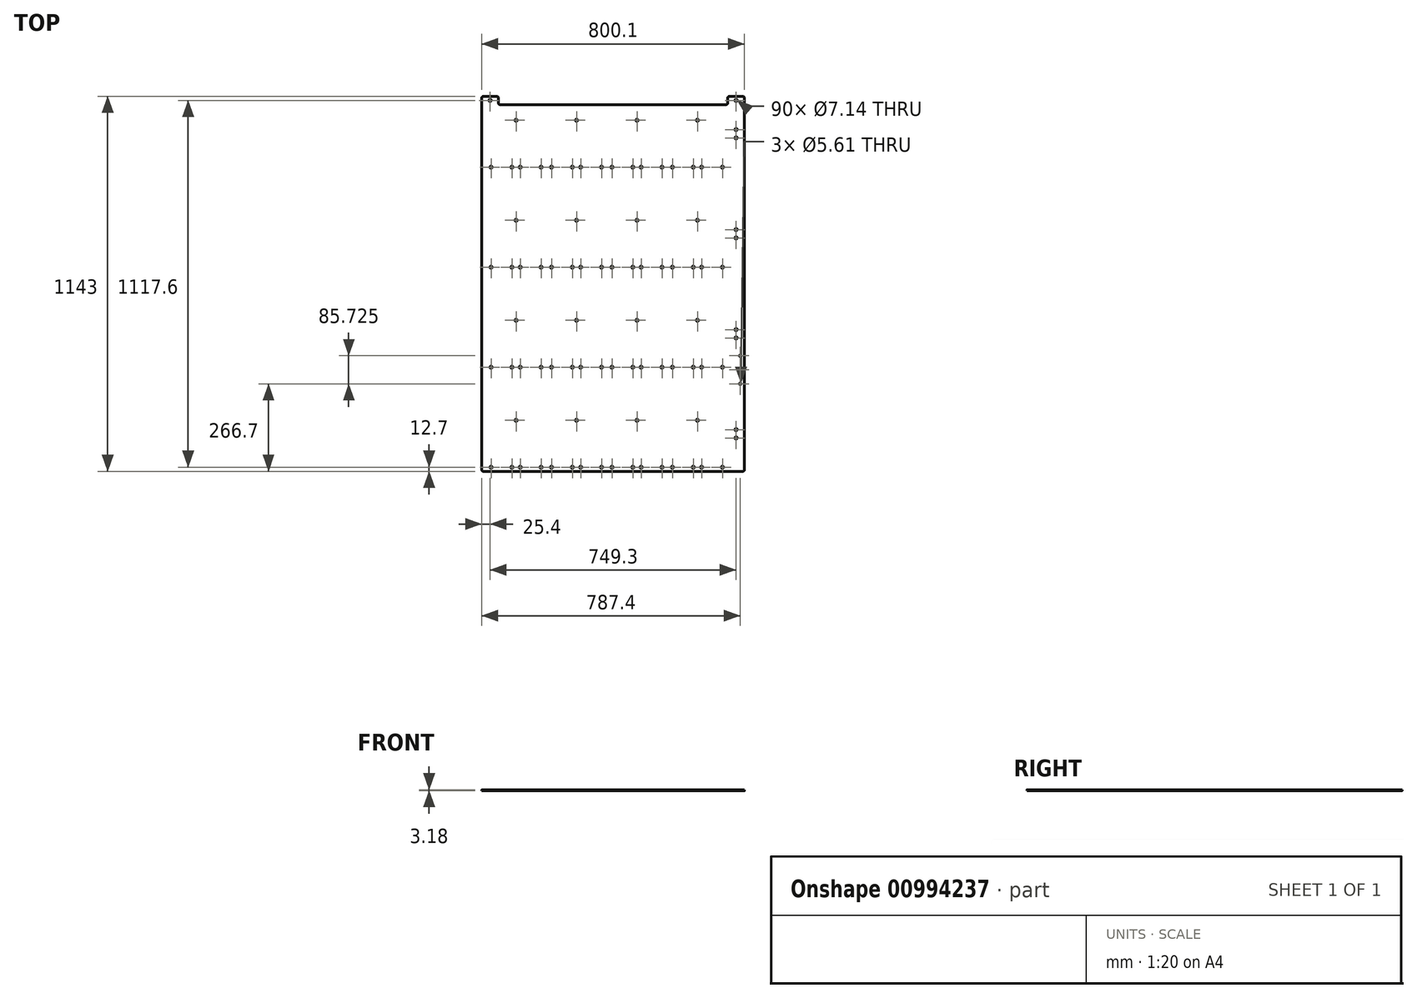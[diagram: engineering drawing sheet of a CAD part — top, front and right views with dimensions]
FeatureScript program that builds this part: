
annotation { "Feature Type Name" : "Feature", "Feature Type Description" : "" }
export const myFeature = defineFeature(function(context is Context, id is Id, definition is map)
    precondition{}
    {
        {
            var Q0;
            Q0=qCreatedBy(makeId("Top.planeOp"),FACE);
            var sketch = newSketch(context, id + "F0", { "sketchPlane" : qUnion([Q0])});
            skLineSegment(sketch, "E0.bottom", {"start": v(0, 0) * mm, "end": v(800.1, 0) * mm});
            skLineSegment(sketch, "E0.top", {"start": v(0, 1181.1) * mm, "end": v(800.1, 1181.1) * mm});
            skLineSegment(sketch, "E0.left", {"start": v(0, 0) * mm, "end": v(0, 1181.1) * mm});
            skLineSegment(sketch, "E0.right", {"start": v(800.1, 0) * mm, "end": v(800.1, 1181.1) * mm});
            skLineSegment(sketch, "E1", {"start": v(25.4, 1181.1) * mm, "end": v(25.4, 0) * mm, "construction": true});
            skLineSegment(sketch, "E2", {"start": v(698.5, 1181.1) * mm, "end": v(698.5, 0) * mm, "construction": true});
            skLineSegment(sketch, "E3", {"start": v(0, 1155.7) * mm, "end": v(800.1, 1155.7) * mm, "construction": true});
            skLineSegment(sketch, "E4", {"start": v(0, 571.5) * mm, "end": v(800.1, 571.5) * mm, "construction": true});
            skLineSegment(sketch, "E5", {"start": v(0, 279.4) * mm, "end": v(800.1, 279.4) * mm, "construction": true});
            skPoint(sketch, "E6", {"position": v(92.08, 965.2) * mm});
            skPoint(sketch, "E7.0.1.0", {"position": v(92.08, 660.4) * mm});
            skPoint(sketch, "E7.0.2.0", {"position": v(92.08, 355.6) * mm});
            skPoint(sketch, "E7.0.3.0", {"position": v(92.08, 50.8) * mm});
            skPoint(sketch, "E7.1.0.0", {"position": v(276.23, 965.2) * mm});
            skPoint(sketch, "E7.1.1.0", {"position": v(276.23, 660.4) * mm});
            skPoint(sketch, "E7.1.2.0", {"position": v(276.23, 355.6) * mm});
            skPoint(sketch, "E7.1.3.0", {"position": v(276.23, 50.8) * mm});
            skPoint(sketch, "E7.2.0.0", {"position": v(460.38, 965.2) * mm});
            skPoint(sketch, "E7.2.1.0", {"position": v(460.38, 660.4) * mm});
            skPoint(sketch, "E7.2.2.0", {"position": v(460.38, 355.6) * mm});
            skPoint(sketch, "E7.2.3.0", {"position": v(460.38, 50.8) * mm});
            skPoint(sketch, "E7.3.0.0", {"position": v(644.52, 965.2) * mm});
            skPoint(sketch, "E7.3.1.0", {"position": v(644.52, 660.4) * mm});
            skPoint(sketch, "E7.3.2.0", {"position": v(644.53, 355.6) * mm});
            skPoint(sketch, "E7.3.3.0", {"position": v(644.53, 50.8) * mm});
            skLineSegment(sketch, "E7.direction1", {"start": v(92.08, 965.2) * mm, "end": v(276.23, 965.2) * mm, "construction": true});
            skLineSegment(sketch, "E7.direction2", {"start": v(92.08, 965.2) * mm, "end": v(92.08, 660.4) * mm, "construction": true});
            skPoint(sketch, "E8", {"position": v(117.48, 965.2) * mm});
            skPoint(sketch, "E9.0.1.0", {"position": v(117.48, 660.4) * mm});
            skPoint(sketch, "E9.0.2.0", {"position": v(117.48, 355.6) * mm});
            skPoint(sketch, "E9.0.3.0", {"position": v(117.48, 50.8) * mm});
            skPoint(sketch, "E9.1.0.0", {"position": v(301.63, 965.2) * mm});
            skPoint(sketch, "E9.1.1.0", {"position": v(301.63, 660.4) * mm});
            skPoint(sketch, "E9.1.2.0", {"position": v(301.63, 355.6) * mm});
            skPoint(sketch, "E9.1.3.0", {"position": v(301.63, 50.8) * mm});
            skPoint(sketch, "E9.2.0.0", {"position": v(485.78, 965.2) * mm});
            skPoint(sketch, "E9.2.1.0", {"position": v(485.78, 660.4) * mm});
            skPoint(sketch, "E9.2.2.0", {"position": v(485.78, 355.6) * mm});
            skPoint(sketch, "E9.2.3.0", {"position": v(485.78, 50.8) * mm});
            skPoint(sketch, "E9.3.0.0", {"position": v(669.92, 965.2) * mm});
            skPoint(sketch, "E9.3.1.0", {"position": v(669.92, 660.4) * mm});
            skPoint(sketch, "E9.3.2.0", {"position": v(669.93, 355.6) * mm});
            skPoint(sketch, "E9.3.3.0", {"position": v(669.93, 50.8) * mm});
            skLineSegment(sketch, "E9.direction1", {"start": v(117.48, 965.2) * mm, "end": v(301.63, 965.2) * mm, "construction": true});
            skLineSegment(sketch, "E9.direction2", {"start": v(117.48, 965.2) * mm, "end": v(117.48, 660.4) * mm, "construction": true});
            skPoint(sketch, "E10", {"position": v(25.4, 1168.4) * mm});
            skPoint(sketch, "E11", {"position": v(774.7, 1168.4) * mm});
            skPoint(sketch, "E12", {"position": v(774.7, 1079.5) * mm});
            skPoint(sketch, "E13", {"position": v(774.7, 1054.1) * mm});
            skPoint(sketch, "E14.0.1.0", {"position": v(774.7, 774.7) * mm});
            skPoint(sketch, "E14.0.1.1", {"position": v(774.7, 749.3) * mm});
            skPoint(sketch, "E14.0.2.0", {"position": v(774.7, 469.9) * mm});
            skPoint(sketch, "E14.0.2.1", {"position": v(774.7, 444.5) * mm});
            skPoint(sketch, "E14.0.3.0", {"position": v(774.7, 165.1) * mm});
            skPoint(sketch, "E14.0.3.1", {"position": v(774.7, 139.7) * mm});
            skLineSegment(sketch, "E14.direction1", {"start": v(774.7, 1054.1) * mm, "end": v(800.1, 1054.1) * mm, "construction": true});
            skLineSegment(sketch, "E14.direction2", {"start": v(774.7, 1054.1) * mm, "end": v(774.7, 749.3) * mm, "construction": true});
            skPoint(sketch, "E15", {"position": v(787.4, 304.8) * mm});
            skPoint(sketch, "E16", {"position": v(787.4, 347.66) * mm});
            skPoint(sketch, "E17", {"position": v(787.4, 390.52) * mm});
            skLineSegment(sketch, "E18", {"start": v(104.77, 1155.7) * mm, "end": v(104.77, 0) * mm, "construction": true});
            skPoint(sketch, "E19", {"position": v(28.57, 965.2) * mm});
            skPoint(sketch, "E20", {"position": v(180.97, 965.2) * mm});
            skPoint(sketch, "E21.0.1.0", {"position": v(28.58, 660.4) * mm});
            skPoint(sketch, "E21.0.1.1", {"position": v(180.98, 660.4) * mm});
            skPoint(sketch, "E21.0.2.0", {"position": v(28.58, 355.6) * mm});
            skPoint(sketch, "E21.0.2.1", {"position": v(180.98, 355.6) * mm});
            skPoint(sketch, "E21.0.3.0", {"position": v(28.58, 50.8) * mm});
            skPoint(sketch, "E21.0.3.1", {"position": v(180.98, 50.8) * mm});
            skPoint(sketch, "E21.1.0.0", {"position": v(212.72, 965.2) * mm});
            skPoint(sketch, "E21.1.0.1", {"position": v(365.13, 965.2) * mm});
            skPoint(sketch, "E21.1.1.0", {"position": v(212.73, 660.4) * mm});
            skPoint(sketch, "E21.1.1.1", {"position": v(365.13, 660.4) * mm});
            skPoint(sketch, "E21.1.2.0", {"position": v(212.73, 355.6) * mm});
            skPoint(sketch, "E21.1.2.1", {"position": v(365.13, 355.6) * mm});
            skPoint(sketch, "E21.1.3.0", {"position": v(212.73, 50.8) * mm});
            skPoint(sketch, "E21.1.3.1", {"position": v(365.13, 50.8) * mm});
            skPoint(sketch, "E21.2.0.0", {"position": v(396.88, 965.2) * mm});
            skPoint(sketch, "E21.2.0.1", {"position": v(549.28, 965.2) * mm});
            skPoint(sketch, "E21.2.1.0", {"position": v(396.88, 660.4) * mm});
            skPoint(sketch, "E21.2.1.1", {"position": v(549.28, 660.4) * mm});
            skPoint(sketch, "E21.2.2.0", {"position": v(396.88, 355.6) * mm});
            skPoint(sketch, "E21.2.2.1", {"position": v(549.28, 355.6) * mm});
            skPoint(sketch, "E21.2.3.0", {"position": v(396.88, 50.8) * mm});
            skPoint(sketch, "E21.2.3.1", {"position": v(549.28, 50.8) * mm});
            skPoint(sketch, "E21.3.0.0", {"position": v(581.03, 965.2) * mm});
            skPoint(sketch, "E21.3.0.1", {"position": v(733.43, 965.2) * mm});
            skPoint(sketch, "E21.3.1.0", {"position": v(581.03, 660.4) * mm});
            skPoint(sketch, "E21.3.1.1", {"position": v(733.43, 660.4) * mm});
            skPoint(sketch, "E21.3.2.0", {"position": v(581.03, 355.6) * mm});
            skPoint(sketch, "E21.3.2.1", {"position": v(733.43, 355.6) * mm});
            skPoint(sketch, "E21.3.3.0", {"position": v(581.03, 50.8) * mm});
            skPoint(sketch, "E21.3.3.1", {"position": v(733.43, 50.8) * mm});
            skLineSegment(sketch, "E21.direction1", {"start": v(28.57, 965.2) * mm, "end": v(212.72, 965.2) * mm, "construction": true});
            skLineSegment(sketch, "E21.direction2", {"start": v(28.57, 965.2) * mm, "end": v(28.57, 660.4) * mm, "construction": true});
            skPoint(sketch, "E22", {"position": v(104.77, 1108.08) * mm});
            skPoint(sketch, "E23.0.1.0", {"position": v(104.78, 803.28) * mm});
            skPoint(sketch, "E23.0.2.0", {"position": v(104.78, 498.48) * mm});
            skPoint(sketch, "E23.0.3.0", {"position": v(104.78, 193.68) * mm});
            skPoint(sketch, "E23.1.0.0", {"position": v(288.93, 1108.08) * mm});
            skPoint(sketch, "E23.1.1.0", {"position": v(288.93, 803.28) * mm});
            skPoint(sketch, "E23.1.2.0", {"position": v(288.93, 498.48) * mm});
            skPoint(sketch, "E23.1.3.0", {"position": v(288.93, 193.68) * mm});
            skPoint(sketch, "E23.2.0.0", {"position": v(473.07, 1108.08) * mm});
            skPoint(sketch, "E23.2.1.0", {"position": v(473.08, 803.28) * mm});
            skPoint(sketch, "E23.2.2.0", {"position": v(473.08, 498.48) * mm});
            skPoint(sketch, "E23.2.3.0", {"position": v(473.08, 193.68) * mm});
            skPoint(sketch, "E23.3.0.0", {"position": v(657.22, 1108.08) * mm});
            skPoint(sketch, "E23.3.1.0", {"position": v(657.22, 803.28) * mm});
            skPoint(sketch, "E23.3.2.0", {"position": v(657.23, 498.48) * mm});
            skPoint(sketch, "E23.3.3.0", {"position": v(657.23, 193.68) * mm});
            skLineSegment(sketch, "E23.direction1", {"start": v(104.77, 1108.08) * mm, "end": v(288.93, 1108.08) * mm, "construction": true});
            skLineSegment(sketch, "E23.direction2", {"start": v(104.77, 1108.08) * mm, "end": v(104.77, 803.28) * mm, "construction": true});
            skLineSegment(sketch, "E24", {"start": v(50.8, 1181.1) * mm, "end": v(50.8, 1155.7) * mm});
            skLineSegment(sketch, "E25", {"start": v(749.3, 1181.1) * mm, "end": v(749.3, 1155.7) * mm});
            skLineSegment(sketch, "E26", {"start": v(749.3, 1155.7) * mm, "end": v(50.8, 1155.7) * mm});
            skLineSegment(sketch, "E27", {"start": v(0, 38.1) * mm, "end": v(800.1, 38.1) * mm});
            skSolve(sketch);
        }
        {
            var Q0;
            {var subQ0=sQuery(id+"F0.wireOp",EDGE,"E0.left");var subQ1=sQuery(id+"F0.wireOp",EDGE,"E0.top");var subQ2=makeQuery(id+"F0.imprint","INTERSECT",VERTEX,{"derivedFrom":[subQ1,subQ0]});Q0=makeQuery(id+"F0.imprint","IMPRINT",FACE,{"disambiguationData":[TD([[makeQuery(id+"F0.imprint","IMPRINT",EDGE,{"disambiguationData":[TD([[subQ2,-1.0]])],"derivedFrom":subQ1}),-1.0]])]});}
            var Q1;
            {var subQ0=sQuery(id+"F0.wireOp",EDGE,"E3");var subQ1=sQuery(id+"F0.wireOp",EDGE,"E1");var subQ2=makeQuery(id+"F0.imprint","INTERSECT",VERTEX,{"derivedFrom":[subQ1,subQ0]});Q1=makeQuery(id+"F0.imprint","IMPRINT",FACE,{"disambiguationData":[TD([[makeQuery(id+"F0.imprint","IMPRINT",EDGE,{"disambiguationData":[TD([[subQ2,-1.0]])],"derivedFrom":subQ1}),1.0]])]});}
            var Q2;
            {var subQ0=sQuery(id+"F0.wireOp",EDGE,"E1");var subQ1=sQuery(id+"F0.wireOp",EDGE,"E0.top");var subQ2=makeQuery(id+"F0.imprint","INTERSECT",VERTEX,{"derivedFrom":[subQ1,subQ0]});Q2=makeQuery(id+"F0.imprint","IMPRINT",FACE,{"disambiguationData":[TD([[makeQuery(id+"F0.imprint","IMPRINT",EDGE,{"disambiguationData":[TD([[subQ2,-1.0]])],"derivedFrom":subQ1}),-1.0]])]});}
            var Q3;
            {var subQ0=sQuery(id+"F0.wireOp",EDGE,"NvVz9uSu-g0Y1-4IFq-BhJ5-FsJu9NIrgNAI");var subQ1=sQuery(id+"F0.wireOp",EDGE,"E0.top");var subQ2=makeQuery(id+"F0.imprint","INTERSECT",VERTEX,{"derivedFrom":[subQ1,subQ0]});Q3=makeQuery(id+"F0.imprint","IMPRINT",FACE,{"disambiguationData":[TD([[makeQuery(id+"F0.imprint","IMPRINT",EDGE,{"disambiguationData":[TD([[subQ2,-1.0]])],"derivedFrom":subQ1}),-1.0]])]});}
            var Q4;
            {var subQ0=sQuery(id+"F0.wireOp",EDGE,"cLlzPfLG-G2uJ-Tusc-6pe5-ku9Q1r7dDU9i");var subQ1=sQuery(id+"F0.wireOp",EDGE,"E0.top");var subQ2=makeQuery(id+"F0.imprint","INTERSECT",VERTEX,{"derivedFrom":[subQ1,subQ0]});Q4=makeQuery(id+"F0.imprint","IMPRINT",FACE,{"disambiguationData":[TD([[makeQuery(id+"F0.imprint","IMPRINT",EDGE,{"disambiguationData":[TD([[subQ2,-1.0]])],"derivedFrom":subQ1}),-1.0]])]});}
            var Q5;
            {var subQ0=sQuery(id+"F0.wireOp",EDGE,"E3");var subQ1=sQuery(id+"F0.wireOp",EDGE,"cLlzPfLG-G2uJ-Tusc-6pe5-ku9Q1r7dDU9i");var subQ2=makeQuery(id+"F0.imprint","INTERSECT",VERTEX,{"derivedFrom":[subQ1,subQ0]});Q5=makeQuery(id+"F0.imprint","IMPRINT",FACE,{"disambiguationData":[TD([[makeQuery(id+"F0.imprint","IMPRINT",EDGE,{"disambiguationData":[TD([[subQ2,-1.0]])],"derivedFrom":subQ1}),1.0]])]});}
            var Q6;
            {var subQ0=sQuery(id+"F0.wireOp",EDGE,"E3");var subQ1=sQuery(id+"F0.wireOp",EDGE,"NvVz9uSu-g0Y1-4IFq-BhJ5-FsJu9NIrgNAI");var subQ2=makeQuery(id+"F0.imprint","INTERSECT",VERTEX,{"derivedFrom":[subQ1,subQ0]});Q6=makeQuery(id+"F0.imprint","IMPRINT",FACE,{"disambiguationData":[TD([[makeQuery(id+"F0.imprint","IMPRINT",EDGE,{"disambiguationData":[TD([[subQ2,-1.0]])],"derivedFrom":subQ1}),1.0]])]});}
            var Q7;
            {var subQ0=sQuery(id+"F0.wireOp",EDGE,"XBvf98FV-Zfnk-rAxB-vRlJ-VYZdYTgvSFKY");var subQ1=sQuery(id+"F0.wireOp",EDGE,"E1");var subQ2=makeQuery(id+"F0.imprint","INTERSECT",VERTEX,{"derivedFrom":[subQ1,subQ0]});Q7=makeQuery(id+"F0.imprint","IMPRINT",FACE,{"disambiguationData":[TD([[makeQuery(id+"F0.imprint","IMPRINT",EDGE,{"disambiguationData":[TD([[subQ2,-1.0]])],"derivedFrom":subQ1}),1.0]])]});}
            var Q8;
            {var subQ0=sQuery(id+"F0.wireOp",EDGE,"XBvf98FV-Zfnk-rAxB-vRlJ-VYZdYTgvSFKY");var subQ1=sQuery(id+"F0.wireOp",EDGE,"NvVz9uSu-g0Y1-4IFq-BhJ5-FsJu9NIrgNAI");var subQ2=makeQuery(id+"F0.imprint","INTERSECT",VERTEX,{"derivedFrom":[subQ1,subQ0]});Q8=makeQuery(id+"F0.imprint","IMPRINT",FACE,{"disambiguationData":[TD([[makeQuery(id+"F0.imprint","IMPRINT",EDGE,{"disambiguationData":[TD([[subQ2,-1.0]])],"derivedFrom":subQ1}),1.0]])]});}
            var Q9;
            {var subQ0=sQuery(id+"F0.wireOp",EDGE,"XBvf98FV-Zfnk-rAxB-vRlJ-VYZdYTgvSFKY");var subQ1=sQuery(id+"F0.wireOp",EDGE,"cLlzPfLG-G2uJ-Tusc-6pe5-ku9Q1r7dDU9i");var subQ2=makeQuery(id+"F0.imprint","INTERSECT",VERTEX,{"derivedFrom":[subQ1,subQ0]});Q9=makeQuery(id+"F0.imprint","IMPRINT",FACE,{"disambiguationData":[TD([[makeQuery(id+"F0.imprint","IMPRINT",EDGE,{"disambiguationData":[TD([[subQ2,-1.0]])],"derivedFrom":subQ1}),1.0]])]});}
            var Q10;
            {var subQ0=sQuery(id+"F0.wireOp",EDGE,"E4");var subQ1=sQuery(id+"F0.wireOp",EDGE,"E1");var subQ2=makeQuery(id+"F0.imprint","INTERSECT",VERTEX,{"derivedFrom":[subQ1,subQ0]});Q10=makeQuery(id+"F0.imprint","IMPRINT",FACE,{"disambiguationData":[TD([[makeQuery(id+"F0.imprint","IMPRINT",EDGE,{"disambiguationData":[TD([[subQ2,-1.0]])],"derivedFrom":subQ1}),1.0]])]});}
            var Q11;
            {var subQ0=sQuery(id+"F0.wireOp",EDGE,"E4");var subQ1=sQuery(id+"F0.wireOp",EDGE,"cLlzPfLG-G2uJ-Tusc-6pe5-ku9Q1r7dDU9i");var subQ2=makeQuery(id+"F0.imprint","INTERSECT",VERTEX,{"derivedFrom":[subQ1,subQ0]});Q11=makeQuery(id+"F0.imprint","IMPRINT",FACE,{"disambiguationData":[TD([[makeQuery(id+"F0.imprint","IMPRINT",EDGE,{"disambiguationData":[TD([[subQ2,-1.0]])],"derivedFrom":subQ1}),1.0]])]});}
            var Q12;
            {var subQ0=sQuery(id+"F0.wireOp",EDGE,"E4");var subQ1=sQuery(id+"F0.wireOp",EDGE,"NvVz9uSu-g0Y1-4IFq-BhJ5-FsJu9NIrgNAI");var subQ2=makeQuery(id+"F0.imprint","INTERSECT",VERTEX,{"derivedFrom":[subQ1,subQ0]});Q12=makeQuery(id+"F0.imprint","IMPRINT",FACE,{"disambiguationData":[TD([[makeQuery(id+"F0.imprint","IMPRINT",EDGE,{"disambiguationData":[TD([[subQ2,-1.0]])],"derivedFrom":subQ1}),1.0]])]});}
            var Q13;
            {var subQ0=sQuery(id+"F0.wireOp",EDGE,"E4");var subQ1=sQuery(id+"F0.wireOp",EDGE,"7kM9J1mK-a5lG-o4nB-CUha-a5kKUpg4Ji5t");var subQ2=makeQuery(id+"F0.imprint","INTERSECT",VERTEX,{"derivedFrom":[subQ1,subQ0]});Q13=makeQuery(id+"F0.imprint","IMPRINT",FACE,{"disambiguationData":[TD([[makeQuery(id+"F0.imprint","IMPRINT",EDGE,{"disambiguationData":[TD([[subQ2,-1.0]])],"derivedFrom":subQ1}),1.0]])]});}
            var Q14;
            {var subQ0=sQuery(id+"F0.wireOp",EDGE,"E4");var subQ1=sQuery(id+"F0.wireOp",EDGE,"z4tCeGBH-dsUb-3HiC-7aPG-VEvBwGlrVRZZ");var subQ2=makeQuery(id+"F0.imprint","INTERSECT",VERTEX,{"derivedFrom":[subQ1,subQ0]});Q14=makeQuery(id+"F0.imprint","IMPRINT",FACE,{"disambiguationData":[TD([[makeQuery(id+"F0.imprint","IMPRINT",EDGE,{"disambiguationData":[TD([[subQ2,-1.0]])],"derivedFrom":subQ1}),1.0]])]});}
            var Q15;
            {var subQ0=sQuery(id+"F0.wireOp",EDGE,"XBvf98FV-Zfnk-rAxB-vRlJ-VYZdYTgvSFKY");var subQ1=sQuery(id+"F0.wireOp",EDGE,"z4tCeGBH-dsUb-3HiC-7aPG-VEvBwGlrVRZZ");var subQ2=makeQuery(id+"F0.imprint","INTERSECT",VERTEX,{"derivedFrom":[subQ1,subQ0]});Q15=makeQuery(id+"F0.imprint","IMPRINT",FACE,{"disambiguationData":[TD([[makeQuery(id+"F0.imprint","IMPRINT",EDGE,{"disambiguationData":[TD([[subQ2,-1.0]])],"derivedFrom":subQ1}),1.0]])]});}
            var Q16;
            {var subQ0=sQuery(id+"F0.wireOp",EDGE,"XBvf98FV-Zfnk-rAxB-vRlJ-VYZdYTgvSFKY");var subQ1=sQuery(id+"F0.wireOp",EDGE,"7kM9J1mK-a5lG-o4nB-CUha-a5kKUpg4Ji5t");var subQ2=makeQuery(id+"F0.imprint","INTERSECT",VERTEX,{"derivedFrom":[subQ1,subQ0]});Q16=makeQuery(id+"F0.imprint","IMPRINT",FACE,{"disambiguationData":[TD([[makeQuery(id+"F0.imprint","IMPRINT",EDGE,{"disambiguationData":[TD([[subQ2,-1.0]])],"derivedFrom":subQ1}),1.0]])]});}
            var Q17;
            {var subQ0=sQuery(id+"F0.wireOp",EDGE,"7kM9J1mK-a5lG-o4nB-CUha-a5kKUpg4Ji5t");var subQ1=sQuery(id+"F0.wireOp",EDGE,"E0.top");var subQ2=makeQuery(id+"F0.imprint","INTERSECT",VERTEX,{"derivedFrom":[subQ1,subQ0]});Q17=makeQuery(id+"F0.imprint","IMPRINT",FACE,{"disambiguationData":[TD([[makeQuery(id+"F0.imprint","IMPRINT",EDGE,{"disambiguationData":[TD([[subQ2,-1.0]])],"derivedFrom":subQ1}),-1.0]])]});}
            var Q18;
            {var subQ0=sQuery(id+"F0.wireOp",EDGE,"E3");var subQ1=sQuery(id+"F0.wireOp",EDGE,"7kM9J1mK-a5lG-o4nB-CUha-a5kKUpg4Ji5t");var subQ2=makeQuery(id+"F0.imprint","INTERSECT",VERTEX,{"derivedFrom":[subQ1,subQ0]});Q18=makeQuery(id+"F0.imprint","IMPRINT",FACE,{"disambiguationData":[TD([[makeQuery(id+"F0.imprint","IMPRINT",EDGE,{"disambiguationData":[TD([[subQ2,-1.0]])],"derivedFrom":subQ1}),1.0]])]});}
            var Q19;
            {var subQ0=sQuery(id+"F0.wireOp",EDGE,"E3");var subQ1=sQuery(id+"F0.wireOp",EDGE,"z4tCeGBH-dsUb-3HiC-7aPG-VEvBwGlrVRZZ");var subQ2=makeQuery(id+"F0.imprint","INTERSECT",VERTEX,{"derivedFrom":[subQ1,subQ0]});Q19=makeQuery(id+"F0.imprint","IMPRINT",FACE,{"disambiguationData":[TD([[makeQuery(id+"F0.imprint","IMPRINT",EDGE,{"disambiguationData":[TD([[subQ2,-1.0]])],"derivedFrom":subQ1}),1.0]])]});}
            var Q20;
            {var subQ0=sQuery(id+"F0.wireOp",EDGE,"z4tCeGBH-dsUb-3HiC-7aPG-VEvBwGlrVRZZ");var subQ1=sQuery(id+"F0.wireOp",EDGE,"E0.top");var subQ2=makeQuery(id+"F0.imprint","INTERSECT",VERTEX,{"derivedFrom":[subQ1,subQ0]});Q20=makeQuery(id+"F0.imprint","IMPRINT",FACE,{"disambiguationData":[TD([[makeQuery(id+"F0.imprint","IMPRINT",EDGE,{"disambiguationData":[TD([[subQ2,-1.0]])],"derivedFrom":subQ1}),-1.0]])]});}
            var Q21;
            {var subQ0=sQuery(id+"F0.wireOp",EDGE,"E3");var subQ1=sQuery(id+"F0.wireOp",EDGE,"je7lqKF7-A4vJ-4WHE-x7hp-U7TIOAv7D40W");var subQ2=makeQuery(id+"F0.imprint","INTERSECT",VERTEX,{"derivedFrom":[subQ1,subQ0]});Q21=makeQuery(id+"F0.imprint","IMPRINT",FACE,{"disambiguationData":[TD([[makeQuery(id+"F0.imprint","IMPRINT",EDGE,{"disambiguationData":[TD([[subQ2,-1.0]])],"derivedFrom":subQ1}),1.0]])]});}
            var Q22;
            {var subQ0=sQuery(id+"F0.wireOp",EDGE,"je7lqKF7-A4vJ-4WHE-x7hp-U7TIOAv7D40W");var subQ1=sQuery(id+"F0.wireOp",EDGE,"E0.top");var subQ2=makeQuery(id+"F0.imprint","INTERSECT",VERTEX,{"derivedFrom":[subQ1,subQ0]});Q22=makeQuery(id+"F0.imprint","IMPRINT",FACE,{"disambiguationData":[TD([[makeQuery(id+"F0.imprint","IMPRINT",EDGE,{"disambiguationData":[TD([[subQ2,-1.0]])],"derivedFrom":subQ1}),-1.0]])]});}
            var Q23;
            {var subQ0=sQuery(id+"F0.wireOp",EDGE,"E0.right");var subQ1=sQuery(id+"F0.wireOp",EDGE,"E0.top");var subQ2=makeQuery(id+"F0.imprint","INTERSECT",VERTEX,{"derivedFrom":[subQ1,subQ0]});Q23=makeQuery(id+"F0.imprint","IMPRINT",FACE,{"disambiguationData":[TD([[makeQuery(id+"F0.imprint","IMPRINT",EDGE,{"disambiguationData":[TD([[subQ2,1.0]])],"derivedFrom":subQ1}),-1.0]])]});}
            var Q24;
            {var subQ0=sQuery(id+"F0.wireOp",EDGE,"oV7xkkTq-LSOp-9kFR-CaCk-h1aCnj0FRsLf");var subQ1=sQuery(id+"F0.wireOp",EDGE,"E0.top");var subQ2=makeQuery(id+"F0.imprint","INTERSECT",VERTEX,{"derivedFrom":[subQ1,subQ0]});Q24=makeQuery(id+"F0.imprint","IMPRINT",FACE,{"disambiguationData":[TD([[makeQuery(id+"F0.imprint","IMPRINT",EDGE,{"disambiguationData":[TD([[subQ2,-1.0]])],"derivedFrom":subQ1}),-1.0]])]});}
            var Q25;
            {var subQ0=sQuery(id+"F0.wireOp",EDGE,"E3");var subQ1=sQuery(id+"F0.wireOp",EDGE,"oV7xkkTq-LSOp-9kFR-CaCk-h1aCnj0FRsLf");var subQ2=makeQuery(id+"F0.imprint","INTERSECT",VERTEX,{"derivedFrom":[subQ1,subQ0]});Q25=makeQuery(id+"F0.imprint","IMPRINT",FACE,{"disambiguationData":[TD([[makeQuery(id+"F0.imprint","IMPRINT",EDGE,{"disambiguationData":[TD([[subQ2,-1.0]])],"derivedFrom":subQ1}),1.0]])]});}
            var Q26;
            {var subQ0=sQuery(id+"F0.wireOp",EDGE,"E4");var subQ1=sQuery(id+"F0.wireOp",EDGE,"je7lqKF7-A4vJ-4WHE-x7hp-U7TIOAv7D40W");var subQ2=makeQuery(id+"F0.imprint","INTERSECT",VERTEX,{"derivedFrom":[subQ1,subQ0]});Q26=makeQuery(id+"F0.imprint","IMPRINT",FACE,{"disambiguationData":[TD([[makeQuery(id+"F0.imprint","IMPRINT",EDGE,{"disambiguationData":[TD([[subQ2,-1.0]])],"derivedFrom":subQ1}),1.0]])]});}
            var Q27;
            {var subQ0=sQuery(id+"F0.wireOp",EDGE,"XBvf98FV-Zfnk-rAxB-vRlJ-VYZdYTgvSFKY");var subQ1=sQuery(id+"F0.wireOp",EDGE,"je7lqKF7-A4vJ-4WHE-x7hp-U7TIOAv7D40W");var subQ2=makeQuery(id+"F0.imprint","INTERSECT",VERTEX,{"derivedFrom":[subQ1,subQ0]});Q27=makeQuery(id+"F0.imprint","IMPRINT",FACE,{"disambiguationData":[TD([[makeQuery(id+"F0.imprint","IMPRINT",EDGE,{"disambiguationData":[TD([[subQ2,-1.0]])],"derivedFrom":subQ1}),1.0]])]});}
            var Q28;
            {var subQ0=sQuery(id+"F0.wireOp",EDGE,"XBvf98FV-Zfnk-rAxB-vRlJ-VYZdYTgvSFKY");var subQ1=sQuery(id+"F0.wireOp",EDGE,"oV7xkkTq-LSOp-9kFR-CaCk-h1aCnj0FRsLf");var subQ2=makeQuery(id+"F0.imprint","INTERSECT",VERTEX,{"derivedFrom":[subQ1,subQ0]});Q28=makeQuery(id+"F0.imprint","IMPRINT",FACE,{"disambiguationData":[TD([[makeQuery(id+"F0.imprint","IMPRINT",EDGE,{"disambiguationData":[TD([[subQ2,-1.0]])],"derivedFrom":subQ1}),1.0]])]});}
            var Q29;
            {var subQ0=sQuery(id+"F0.wireOp",EDGE,"E4");var subQ1=sQuery(id+"F0.wireOp",EDGE,"oV7xkkTq-LSOp-9kFR-CaCk-h1aCnj0FRsLf");var subQ2=makeQuery(id+"F0.imprint","INTERSECT",VERTEX,{"derivedFrom":[subQ1,subQ0]});Q29=makeQuery(id+"F0.imprint","IMPRINT",FACE,{"disambiguationData":[TD([[makeQuery(id+"F0.imprint","IMPRINT",EDGE,{"disambiguationData":[TD([[subQ2,-1.0]])],"derivedFrom":subQ1}),1.0]])]});}
            extrude(context, id + "F1", {"entities" : qUnion([Q0, Q1, Q2, Q3, Q4, Q5, Q6, Q7, Q8, Q9, Q10, Q11, Q12, Q13, Q14, Q15, Q16, Q17, Q18, Q19, Q20, Q21, Q22, Q23, Q24, Q25, Q26, Q27, Q28, Q29]), "depth" : 3.17 * mm, "offsetDistance" : 25.4 * mm});
        }
        {
            var Q0;
            Q0=sQuery(id+"F0.wireOp",VERTEX,"E10");
            var Q1;
            Q1=sQuery(id+"F0.wireOp",VERTEX,"E6");
            var Q2;
            Q2=sQuery(id+"F0.wireOp",VERTEX,"E8");
            var Q3;
            Q3=sQuery(id+"F0.wireOp",VERTEX,"E7.1.0.0");
            var Q4;
            Q4=sQuery(id+"F0.wireOp",VERTEX,"E9.1.0.0");
            var Q5;
            Q5=sQuery(id+"F0.wireOp",VERTEX,"E7.2.0.0");
            var Q6;
            Q6=sQuery(id+"F0.wireOp",VERTEX,"E9.2.0.0");
            var Q7;
            Q7=sQuery(id+"F0.wireOp",VERTEX,"E7.3.0.0");
            var Q8;
            Q8=sQuery(id+"F0.wireOp",VERTEX,"E9.3.0.0");
            var Q9;
            Q9=sQuery(id+"F0.wireOp",VERTEX,"E11");
            var Q10;
            Q10=sQuery(id+"F0.wireOp",VERTEX,"E9.3.1.0");
            var Q11;
            Q11=sQuery(id+"F0.wireOp",VERTEX,"E7.3.1.0");
            var Q12;
            Q12=sQuery(id+"F0.wireOp",VERTEX,"E9.2.1.0");
            var Q13;
            Q13=sQuery(id+"F0.wireOp",VERTEX,"E7.2.1.0");
            var Q14;
            Q14=sQuery(id+"F0.wireOp",VERTEX,"E9.1.1.0");
            var Q15;
            Q15=sQuery(id+"F0.wireOp",VERTEX,"E7.1.1.0");
            var Q16;
            Q16=sQuery(id+"F0.wireOp",VERTEX,"E9.0.1.0");
            var Q17;
            Q17=sQuery(id+"F0.wireOp",VERTEX,"E7.0.1.0");
            var Q18;
            Q18=sQuery(id+"F0.wireOp",VERTEX,"E7.0.2.0");
            var Q19;
            Q19=sQuery(id+"F0.wireOp",VERTEX,"E9.0.2.0");
            var Q20;
            Q20=sQuery(id+"F0.wireOp",VERTEX,"E7.1.2.0");
            var Q21;
            Q21=sQuery(id+"F0.wireOp",VERTEX,"E9.1.2.0");
            var Q22;
            Q22=sQuery(id+"F0.wireOp",VERTEX,"E7.2.2.0");
            var Q23;
            Q23=sQuery(id+"F0.wireOp",VERTEX,"E9.2.2.0");
            var Q24;
            Q24=sQuery(id+"F0.wireOp",VERTEX,"E7.3.2.0");
            var Q25;
            Q25=sQuery(id+"F0.wireOp",VERTEX,"E9.3.2.0");
            var Q26;
            Q26=sQuery(id+"F0.wireOp",VERTEX,"E9.3.3.0");
            var Q27;
            Q27=sQuery(id+"F0.wireOp",VERTEX,"E7.3.3.0");
            var Q28;
            Q28=sQuery(id+"F0.wireOp",VERTEX,"E9.2.3.0");
            var Q29;
            Q29=sQuery(id+"F0.wireOp",VERTEX,"E7.2.3.0");
            var Q30;
            Q30=sQuery(id+"F0.wireOp",VERTEX,"E9.1.3.0");
            var Q31;
            Q31=sQuery(id+"F0.wireOp",VERTEX,"E7.1.3.0");
            var Q32;
            Q32=sQuery(id+"F0.wireOp",VERTEX,"E9.0.3.0");
            var Q33;
            Q33=sQuery(id+"F0.wireOp",VERTEX,"E7.0.3.0");
            var Q34;
            Q34=sQuery(id+"F0.wireOp",VERTEX,"E12");
            var Q35;
            Q35=sQuery(id+"F0.wireOp",VERTEX,"E13");
            var Q36;
            Q36=sQuery(id+"F0.wireOp",VERTEX,"E14.0.1.0");
            var Q37;
            Q37=sQuery(id+"F0.wireOp",VERTEX,"E14.0.1.1");
            var Q38;
            Q38=sQuery(id+"F0.wireOp",VERTEX,"E14.0.2.0");
            var Q39;
            Q39=sQuery(id+"F0.wireOp",VERTEX,"E14.0.2.1");
            var Q40;
            Q40=sQuery(id+"F0.wireOp",VERTEX,"E14.0.3.0");
            var Q41;
            Q41=sQuery(id+"F0.wireOp",VERTEX,"E14.0.3.1");
            var Q42;
            Q42=sQuery(id+"F0.wireOp",VERTEX,"E20");
            var Q43;
            Q43=sQuery(id+"F0.wireOp",VERTEX,"E19");
            var Q44;
            Q44=sQuery(id+"F0.wireOp",VERTEX,"E21.1.0.0");
            var Q45;
            Q45=sQuery(id+"F0.wireOp",VERTEX,"E22");
            var Q46;
            Q46=sQuery(id+"F0.wireOp",VERTEX,"E23.1.0.0");
            var Q47;
            Q47=sQuery(id+"F0.wireOp",VERTEX,"E21.1.0.1");
            var Q48;
            Q48=sQuery(id+"F0.wireOp",VERTEX,"E21.2.0.0");
            var Q49;
            Q49=sQuery(id+"F0.wireOp",VERTEX,"E23.2.0.0");
            var Q50;
            Q50=sQuery(id+"F0.wireOp",VERTEX,"E21.2.0.1");
            var Q51;
            Q51=sQuery(id+"F0.wireOp",VERTEX,"E21.3.0.0");
            var Q52;
            Q52=sQuery(id+"F0.wireOp",VERTEX,"E23.3.0.0");
            var Q53;
            Q53=sQuery(id+"F0.wireOp",VERTEX,"E21.3.0.1");
            var Q54;
            Q54=sQuery(id+"F0.wireOp",VERTEX,"E23.3.1.0");
            var Q55;
            Q55=sQuery(id+"F0.wireOp",VERTEX,"E23.2.1.0");
            var Q56;
            Q56=sQuery(id+"F0.wireOp",VERTEX,"E23.1.1.0");
            var Q57;
            Q57=sQuery(id+"F0.wireOp",VERTEX,"E23.0.1.0");
            var Q58;
            Q58=sQuery(id+"F0.wireOp",VERTEX,"E21.0.1.0");
            var Q59;
            Q59=sQuery(id+"F0.wireOp",VERTEX,"E21.0.1.1");
            var Q60;
            Q60=sQuery(id+"F0.wireOp",VERTEX,"E21.1.1.0");
            var Q61;
            Q61=sQuery(id+"F0.wireOp",VERTEX,"E21.1.1.1");
            var Q62;
            Q62=sQuery(id+"F0.wireOp",VERTEX,"E21.2.1.0");
            var Q63;
            Q63=sQuery(id+"F0.wireOp",VERTEX,"E21.2.1.1");
            var Q64;
            Q64=sQuery(id+"F0.wireOp",VERTEX,"E21.3.1.0");
            var Q65;
            Q65=sQuery(id+"F0.wireOp",VERTEX,"E21.3.1.1");
            var Q66;
            Q66=sQuery(id+"F0.wireOp",VERTEX,"E23.3.2.0");
            var Q67;
            Q67=sQuery(id+"F0.wireOp",VERTEX,"E23.2.2.0");
            var Q68;
            Q68=sQuery(id+"F0.wireOp",VERTEX,"E23.1.2.0");
            var Q69;
            Q69=sQuery(id+"F0.wireOp",VERTEX,"E23.0.2.0");
            var Q70;
            Q70=sQuery(id+"F0.wireOp",VERTEX,"E21.0.2.0");
            var Q71;
            Q71=sQuery(id+"F0.wireOp",VERTEX,"E21.0.2.1");
            var Q72;
            Q72=sQuery(id+"F0.wireOp",VERTEX,"E21.1.2.0");
            var Q73;
            Q73=sQuery(id+"F0.wireOp",VERTEX,"E21.1.2.1");
            var Q74;
            Q74=sQuery(id+"F0.wireOp",VERTEX,"E21.2.2.0");
            var Q75;
            Q75=sQuery(id+"F0.wireOp",VERTEX,"E21.2.2.1");
            var Q76;
            Q76=sQuery(id+"F0.wireOp",VERTEX,"E21.3.2.0");
            var Q77;
            Q77=sQuery(id+"F0.wireOp",VERTEX,"E21.3.2.1");
            var Q78;
            Q78=sQuery(id+"F0.wireOp",VERTEX,"E23.0.3.0");
            var Q79;
            Q79=sQuery(id+"F0.wireOp",VERTEX,"E23.1.3.0");
            var Q80;
            Q80=sQuery(id+"F0.wireOp",VERTEX,"E23.2.3.0");
            var Q81;
            Q81=sQuery(id+"F0.wireOp",VERTEX,"E23.3.3.0");
            var Q82;
            Q82=sQuery(id+"F0.wireOp",VERTEX,"E21.3.3.1");
            var Q83;
            Q83=sQuery(id+"F0.wireOp",VERTEX,"E21.3.3.0");
            var Q84;
            Q84=sQuery(id+"F0.wireOp",VERTEX,"E21.2.3.1");
            var Q85;
            Q85=sQuery(id+"F0.wireOp",VERTEX,"E21.2.3.0");
            var Q86;
            Q86=sQuery(id+"F0.wireOp",VERTEX,"E21.1.3.1");
            var Q87;
            Q87=sQuery(id+"F0.wireOp",VERTEX,"E21.1.3.0");
            var Q88;
            Q88=sQuery(id+"F0.wireOp",VERTEX,"E21.0.3.1");
            var Q89;
            Q89=sQuery(id+"F0.wireOp",VERTEX,"E21.0.3.0");
            var Q90;
            Q90=makeQuery(id+"F1.opExtrude","SWEPT_BODY",BODY,{"disambiguationData":[OSD([sQuery(id+"F0.wireOp",EDGE,"E0.bottom"),sQuery(id+"F0.wireOp",EDGE,"E0.top"),sQuery(id+"F0.wireOp",EDGE,"E0.left"),sQuery(id+"F0.wireOp",EDGE,"E0.right")])]});
            hole(context, id + "F2", {"style" : HoleStyle.SIMPLE, "endStyle" : HoleEndStyle.THROUGH, "oppositeDirection" : true, "standardTappedOrClearance" : lookupTablePath({ "fit" : "Normal (ASME)", "standard" : "ANSI", "size" : "1/4", "type" : "Clearance" }), "standardBlindInLast" : lookupTablePath({ "fit" : "Normal", "standard" : "ANSI", "engagement" : "75%", "pitch" : "20 tpi", "size" : "1/4", "type" : "Clearance & tapped" }), "holeDiameter" : 7.14 * mm, "majorDiameter" : 6.35 * mm, "isTappedThrough" : true, "tappedDepth" : 12.7 * mm, "tapClearance" : 3, "locations" : qUnion([Q0, Q1, Q2, Q3, Q4, Q5, Q6, Q7, Q8, Q9, Q10, Q11, Q12, Q13, Q14, Q15, Q16, Q17, Q18, Q19, Q20, Q21, Q22, Q23, Q24, Q25, Q26, Q27, Q28, Q29, Q30, Q31, Q32, Q33, Q34, Q35, Q36, Q37, Q38, Q39, Q40, Q41, Q42, Q43, Q44, Q45, Q46, Q47, Q48, Q49, Q50, Q51, Q52, Q53, Q54, Q55, Q56, Q57, Q58, Q59, Q60, Q61, Q62, Q63, Q64, Q65, Q66, Q67, Q68, Q69, Q70, Q71, Q72, Q73, Q74, Q75, Q76, Q77, Q78, Q79, Q80, Q81, Q82, Q83, Q84, Q85, Q86, Q87, Q88, Q89]), "scope" : qUnion([Q90])});
        }
        {
            var Q0;
            Q0=makeQuery(id+"F1.opExtrude","SWEPT_EDGE",EDGE,{"disambiguationData":[OSD([sQuery(id+"F0.wireOp",EDGE,"E0.top"),sQuery(id+"F0.wireOp",EDGE,"E0.left")])]});
            var Q1;
            Q1=makeQuery(id+"F1.opExtrude","SWEPT_EDGE",EDGE,{"disambiguationData":[OSD([sQuery(id+"F0.wireOp",EDGE,"E0.top"),sQuery(id+"F0.wireOp",EDGE,"E0.right")])]});
            var Q2;
            Q2=makeQuery(id+"F1.opExtrude","SWEPT_EDGE",EDGE,{"disambiguationData":[OSD([sQuery(id+"F0.wireOp",EDGE,"E0.bottom"),sQuery(id+"F0.wireOp",EDGE,"E0.right")])]});
            var Q3;
            Q3=makeQuery(id+"F1.opExtrude","SWEPT_EDGE",EDGE,{"disambiguationData":[OSD([sQuery(id+"F0.wireOp",EDGE,"E0.bottom"),sQuery(id+"F0.wireOp",EDGE,"E0.left")])]});
            var Q4;
            Q4=makeQuery(id+"F1.opExtrude","SWEPT_EDGE",EDGE,{"disambiguationData":[OSD([sQuery(id+"F0.wireOp",EDGE,"E0.top"),sQuery(id+"F0.wireOp",EDGE,"E24")])]});
            var Q5;
            Q5=makeQuery(id+"F1.opExtrude","SWEPT_EDGE",EDGE,{"disambiguationData":[OSD([sQuery(id+"F0.wireOp",EDGE,"E24"),sQuery(id+"F0.wireOp",EDGE,"E26")])]});
            var Q6;
            Q6=makeQuery(id+"F1.opExtrude","SWEPT_EDGE",EDGE,{"disambiguationData":[OSD([sQuery(id+"F0.wireOp",EDGE,"E25"),sQuery(id+"F0.wireOp",EDGE,"E26")])]});
            var Q7;
            Q7=makeQuery(id+"F1.opExtrude","SWEPT_EDGE",EDGE,{"disambiguationData":[OSD([sQuery(id+"F0.wireOp",EDGE,"E0.top"),sQuery(id+"F0.wireOp",EDGE,"E25")])]});
            fillet(context, id + "F3", {"entities" : qUnion([Q0, Q1, Q2, Q3, Q4, Q5, Q6, Q7]), "radius" : 5.08 * mm, "tangentPropagation" : true, "allowEdgeOverflow" : false});
        }
        {
            var Q0;
            Q0=sQuery(id+"F0.wireOp",VERTEX,"E17");
            var Q1;
            Q1=sQuery(id+"F0.wireOp",VERTEX,"E16");
            var Q2;
            Q2=sQuery(id+"F0.wireOp",VERTEX,"E15");
            var Q3;
            Q3=makeQuery(id+"F1.opExtrude","SWEPT_BODY",BODY,{"disambiguationData":[OSD([sQuery(id+"F0.wireOp",EDGE,"E0.bottom"),sQuery(id+"F0.wireOp",EDGE,"E0.top"),sQuery(id+"F0.wireOp",EDGE,"E0.left"),sQuery(id+"F0.wireOp",EDGE,"E0.right")])]});
            hole(context, id + "F4", {"style" : HoleStyle.SIMPLE, "endStyle" : HoleEndStyle.THROUGH, "oppositeDirection" : true, "standardTappedOrClearance" : lookupTablePath({ "fit" : "Normal (ASME)", "standard" : "ANSI", "size" : "#10", "type" : "Clearance" }), "standardBlindInLast" : lookupTablePath({ "fit" : "Normal", "standard" : "ANSI", "engagement" : "75%", "pitch" : "24 tpi", "size" : "#10", "type" : "Clearance & tapped" }), "holeDiameter" : 5.61 * mm, "majorDiameter" : 6.35 * mm, "isTappedThrough" : true, "tappedDepth" : 12.7 * mm, "tapClearance" : 3, "locations" : qUnion([Q0, Q1, Q2]), "scope" : qUnion([Q3])});
        }
    });
